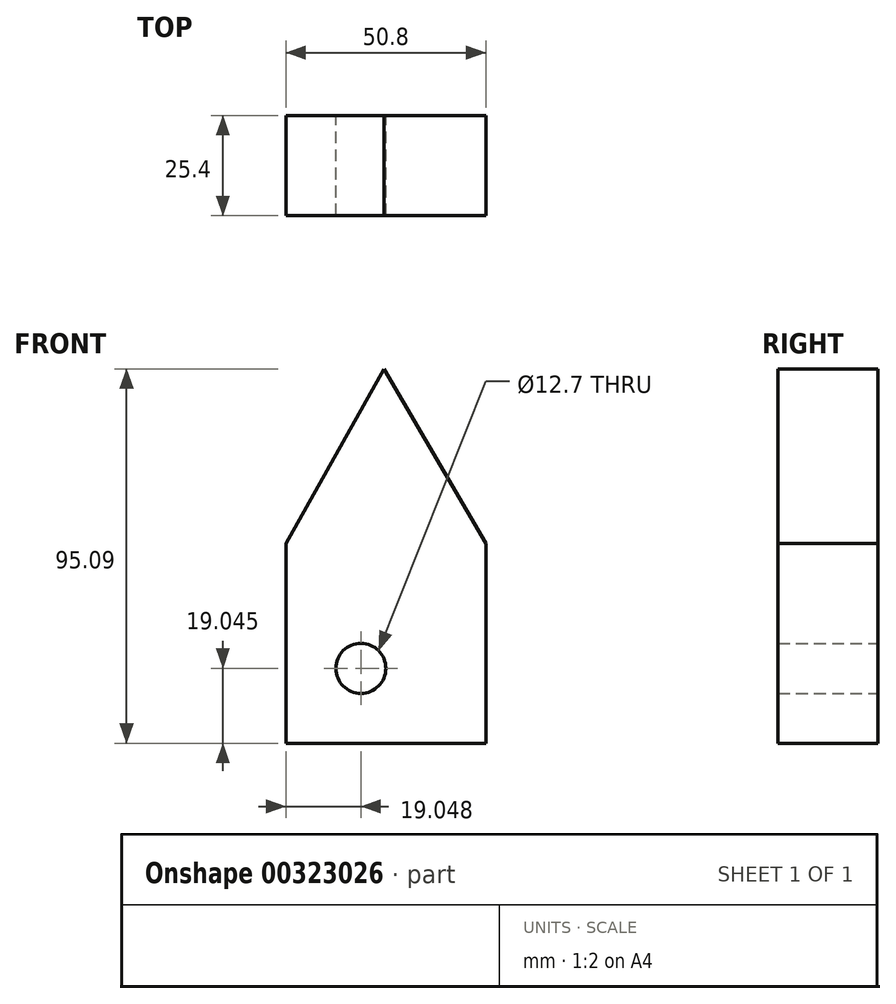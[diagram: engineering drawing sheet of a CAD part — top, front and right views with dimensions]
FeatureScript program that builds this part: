
annotation { "Feature Type Name" : "Feature", "Feature Type Description" : "" }
export const myFeature = defineFeature(function(context is Context, id is Id, definition is map)
    precondition{}
    {
        {
            var Q0;
            Q0=qCreatedBy(makeId("Front.planeOp"),FACE);
            var sketch = newSketch(context, id + "F0", { "sketchPlane" : qUnion([Q0])});
            skLineSegment(sketch, "E0.top", {"start": v(-24.87, -39.21) * mm, "end": v(25.93, -39.21) * mm});
            skLineSegment(sketch, "E0.left", {"start": v(-24.87, 11.59) * mm, "end": v(-24.87, -39.21) * mm});
            skLineSegment(sketch, "E0.right", {"start": v(25.93, 11.59) * mm, "end": v(25.93, -39.21) * mm});
            skLineSegment(sketch, "E1", {"start": v(-24.87, 11.59) * mm, "end": v(0, 55.88) * mm});
            skLineSegment(sketch, "E2", {"start": v(0, 55.88) * mm, "end": v(25.93, 11.59) * mm});
            skCircle(sketch, "E3", {"center": v(-5.82, -20.16) * mm, "radius": 6.35 * mm});
            skSolve(sketch);
        }
        {
            var Q0;
            Q0 = qSketchRegion(id + "F0", true);
            extrude(context, id + "F1", {"entities" : qUnion([Q0]), "depth" : 25.4 * mm});
        }
    });
